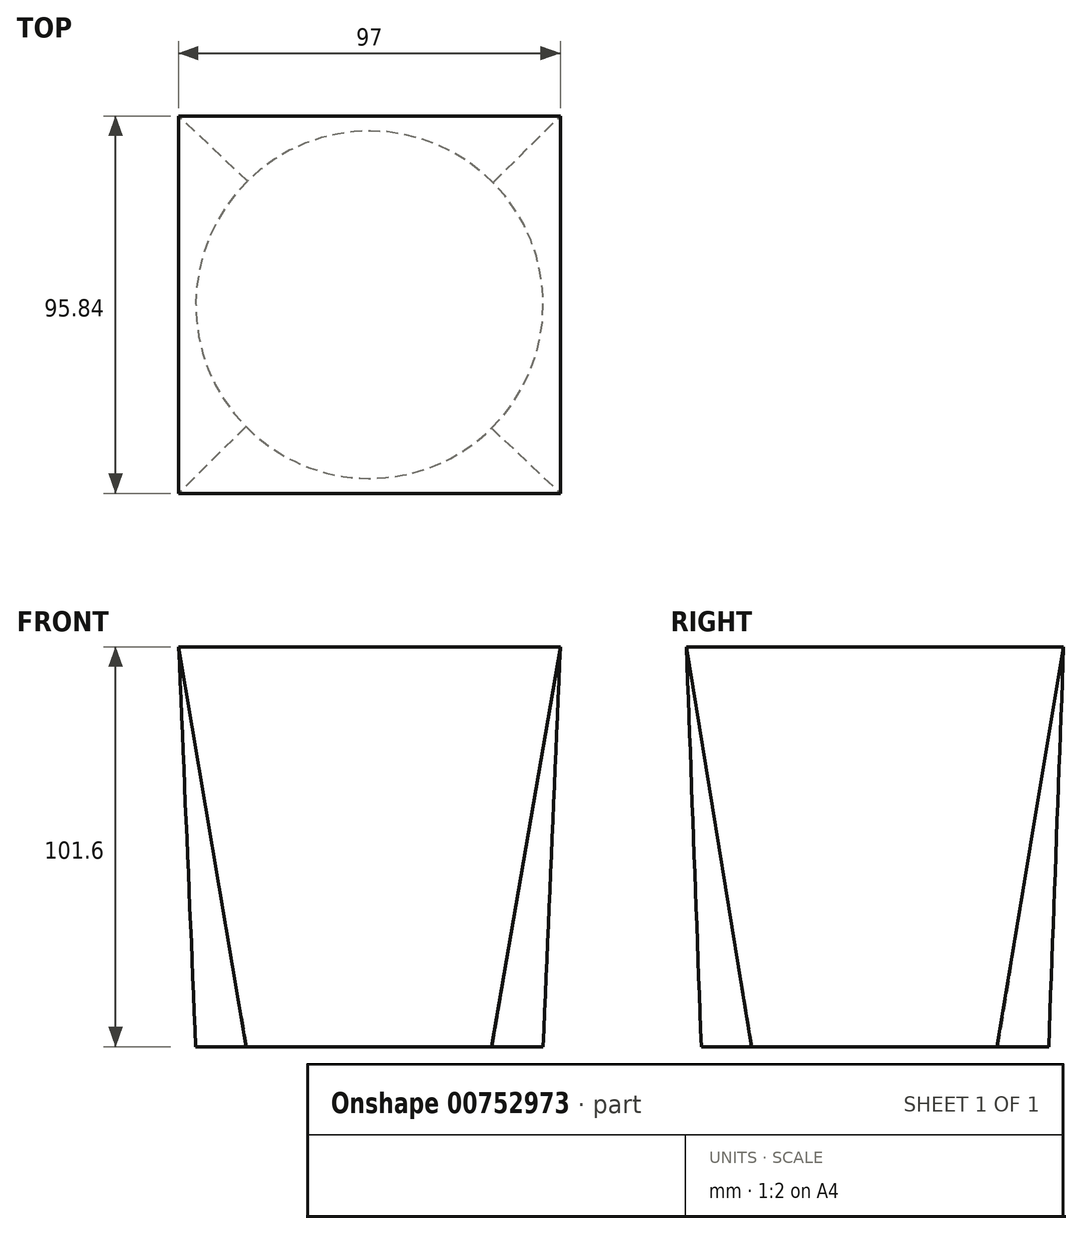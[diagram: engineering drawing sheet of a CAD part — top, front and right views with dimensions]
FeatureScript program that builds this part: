
annotation { "Feature Type Name" : "Feature", "Feature Type Description" : "" }
export const myFeature = defineFeature(function(context is Context, id is Id, definition is map)
    precondition{}
    {
        {
            var Q0;
            Q0=qCreatedBy(makeId("Top.planeOp"),FACE);
            var sketch = newSketch(context, id + "F0", { "sketchPlane" : qUnion([Q0])});
            skCircle(sketch, "E0", {"center": v(0, 0) * mm, "radius": 44.13 * mm});
            skSolve(sketch);
        }
        {
            var Q0;
            Q0=qCreatedBy(makeId("Top.planeOp"),FACE);
            cPlane(context, id + "F1", {"entities" : qUnion([Q0]), "cplaneType" : CPlaneType.OFFSET, "offset" : 101.6 * mm, "width" : 152.4 * mm, "height" : 152.4 * mm});
        }
        {
            var Q0;
            Q0=qCreatedBy(id+"F1.planeOp",FACE);
            var sketch = newSketch(context, id + "F2", { "sketchPlane" : qUnion([Q0])});
            skLineSegment(sketch, "E1.bottom", {"start": v(48.5, 47.92) * mm, "end": v(-48.5, 47.92) * mm});
            skLineSegment(sketch, "E1.top", {"start": v(48.5, -47.92) * mm, "end": v(-48.5, -47.92) * mm});
            skLineSegment(sketch, "E1.left", {"start": v(48.5, 47.92) * mm, "end": v(48.5, -47.92) * mm});
            skLineSegment(sketch, "E1.right", {"start": v(-48.5, 47.92) * mm, "end": v(-48.5, -47.92) * mm});
            skPoint(sketch, "E1.middle", {"position": v(0, 0) * mm});
            skSolve(sketch);
        }
        {
            var Q0;
            Q0=makeQuery(id+"F0.imprint","IMPRINT",FACE,{"disambiguationData":[TD([[makeQuery(id+"F0.imprint","IMPRINT",EDGE,{"derivedFrom":sQuery(id+"F0.wireOp",EDGE,"E0")}),1.0]])]});
            var Q1;
            Q1=makeQuery(id+"F2.imprint","IMPRINT",FACE,{"disambiguationData":[TD([[makeQuery(id+"F2.imprint","IMPRINT",EDGE,{"derivedFrom":sQuery(id+"F2.wireOp",EDGE,"E1.bottom")}),1.0]])]});
            loft(context, id + "F3", {"sheetProfilesArray" : [{ "sheetProfileEntities" : qUnion([Q0]) }, { "sheetProfileEntities" : qUnion([Q1]) }]});
        }
    });
